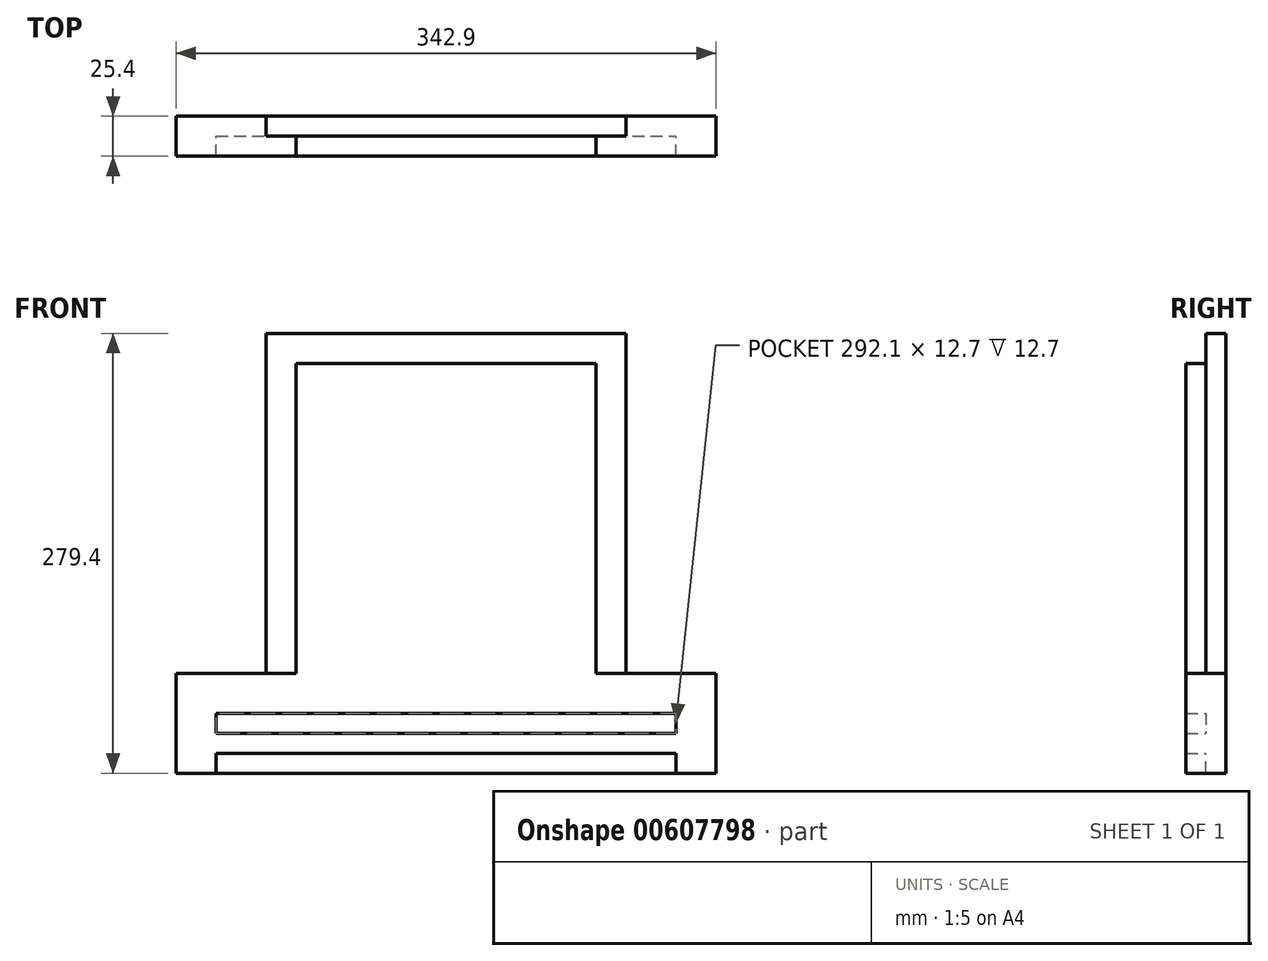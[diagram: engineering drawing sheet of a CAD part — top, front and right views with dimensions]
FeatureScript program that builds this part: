
annotation { "Feature Type Name" : "Feature", "Feature Type Description" : "" }
export const myFeature = defineFeature(function(context is Context, id is Id, definition is map)
    precondition{}
    {
        {
            var Q0;
            Q0=qCreatedBy(makeId("Front.planeOp"),FACE);
            var sketch = newSketch(context, id + "F0", { "sketchPlane" : qUnion([Q0])});
            skLineSegment(sketch, "E0.bottom", {"start": v(0, 0) * mm, "end": v(228.6, 0) * mm});
            skLineSegment(sketch, "E0.top", {"start": v(0, 279.4) * mm, "end": v(228.6, 279.4) * mm});
            skLineSegment(sketch, "E0.left", {"start": v(0, 0) * mm, "end": v(0, 279.4) * mm});
            skLineSegment(sketch, "E0.right", {"start": v(228.6, 0) * mm, "end": v(228.6, 279.4) * mm});
            skSolve(sketch);
        }
        {
            var Q0;
            Q0=makeQuery(id+"F0.imprint","IMPRINT",FACE,{"disambiguationData":[TD([[makeQuery(id+"F0.imprint","IMPRINT",EDGE,{"derivedFrom":sQuery(id+"F0.wireOp",EDGE,"E0.bottom")}),1.0]])]});
            extrude(context, id + "F1", {"entities" : qUnion([Q0]), "depth" : 25.4 * mm, "offsetDistance" : 25.4 * mm});
        }
        {
            var Q0;
            Q0=makeQuery(id+"F1.opExtrude","CAP_FACE",FACE,{"disambiguationData":[OSD([sQuery(id+"F0.wireOp",EDGE,"E0.bottom"),sQuery(id+"F0.wireOp",EDGE,"E0.top"),sQuery(id+"F0.wireOp",EDGE,"E0.left"),sQuery(id+"F0.wireOp",EDGE,"E0.right")])],"isStart":false});
            var sketch = newSketch(context, id + "F2", { "sketchPlane" : qUnion([Q0])});
            skLineSegment(sketch, "E1.bottom", {"start": v(228.6, 0) * mm, "end": v(209.55, 0) * mm});
            skLineSegment(sketch, "E1.top", {"start": v(228.6, 279.4) * mm, "end": v(209.55, 279.4) * mm});
            skLineSegment(sketch, "E1.left", {"start": v(228.6, 0) * mm, "end": v(228.6, 279.4) * mm});
            skLineSegment(sketch, "E1.right", {"start": v(209.55, 0) * mm, "end": v(209.55, 279.4) * mm});
            skSolve(sketch);
        }
        {
            var Q0;
            Q0=makeQuery(id+"F2.imprint","IMPRINT",FACE,{"disambiguationData":[TD([[makeQuery(id+"F2.imprint","IMPRINT",EDGE,{"derivedFrom":sQuery(id+"F2.wireOp",EDGE,"E1.bottom")}),1.0]])]});
            extrude(context, id + "F3", {"entities" : qUnion([Q0]), "operationType" : NewBodyOperationType.REMOVE, "oppositeDirection" : true, "depth" : 12.7 * mm, "offsetDistance" : 25.4 * mm});
        }
        {
            var Q0;
            Q0=makeQuery(id+"F1.opExtrude","CAP_FACE",FACE,{"disambiguationData":[OSD([sQuery(id+"F0.wireOp",EDGE,"E0.bottom"),sQuery(id+"F0.wireOp",EDGE,"E0.top"),sQuery(id+"F0.wireOp",EDGE,"E0.left"),sQuery(id+"F0.wireOp",EDGE,"E0.right")])],"isStart":false});
            var sketch = newSketch(context, id + "F4", { "sketchPlane" : qUnion([Q0])});
            skLineSegment(sketch, "E2.bottom", {"start": v(0, 279.4) * mm, "end": v(19.05, 279.4) * mm});
            skLineSegment(sketch, "E2.top", {"start": v(0, 0) * mm, "end": v(19.05, 0) * mm});
            skLineSegment(sketch, "E2.left", {"start": v(0, 279.4) * mm, "end": v(0, 0) * mm});
            skLineSegment(sketch, "E2.right", {"start": v(19.05, 279.4) * mm, "end": v(19.05, 0) * mm});
            skSolve(sketch);
        }
        {
            var Q0;
            Q0=makeQuery(id+"F4.imprint","IMPRINT",FACE,{"disambiguationData":[TD([[makeQuery(id+"F4.imprint","IMPRINT",EDGE,{"derivedFrom":sQuery(id+"F4.wireOp",EDGE,"E2.bottom")}),-1.0]])]});
            extrude(context, id + "F5", {"entities" : qUnion([Q0]), "operationType" : NewBodyOperationType.REMOVE, "oppositeDirection" : true, "depth" : 12.7 * mm, "offsetDistance" : 25.4 * mm});
        }
        {
            var Q0;
            Q0=makeQuery(id+"F1.opExtrude","CAP_FACE",FACE,{"disambiguationData":[OSD([sQuery(id+"F0.wireOp",EDGE,"E0.bottom"),sQuery(id+"F0.wireOp",EDGE,"E0.top"),sQuery(id+"F0.wireOp",EDGE,"E0.left"),sQuery(id+"F0.wireOp",EDGE,"E0.right")])],"isStart":false});
            var sketch = newSketch(context, id + "F6", { "sketchPlane" : qUnion([Q0])});
            skLineSegment(sketch, "E3.bottom", {"start": v(19.05, 279.4) * mm, "end": v(209.55, 279.4) * mm});
            skLineSegment(sketch, "E3.top", {"start": v(19.05, 260.35) * mm, "end": v(209.55, 260.35) * mm});
            skLineSegment(sketch, "E3.left", {"start": v(19.05, 279.4) * mm, "end": v(19.05, 260.35) * mm});
            skLineSegment(sketch, "E3.right", {"start": v(209.55, 279.4) * mm, "end": v(209.55, 260.35) * mm});
            skSolve(sketch);
        }
        {
            var Q0;
            Q0=makeQuery(id+"F6.imprint","IMPRINT",FACE,{"disambiguationData":[TD([[makeQuery(id+"F6.imprint","IMPRINT",EDGE,{"derivedFrom":sQuery(id+"F6.wireOp",EDGE,"E3.bottom")}),-1.0]])]});
            extrude(context, id + "F7", {"entities" : qUnion([Q0]), "operationType" : NewBodyOperationType.REMOVE, "oppositeDirection" : true, "depth" : 12.7 * mm, "offsetDistance" : 25.4 * mm});
        }
        {
            var Q0;
            Q0=makeQuery(id+"F1.opExtrude","SWEPT_FACE",FACE,{"disambiguationData":[OSD([sQuery(id+"F0.wireOp",EDGE,"E0.right")])]});
            var sketch = newSketch(context, id + "F8", { "sketchPlane" : qUnion([Q0])});
            skLineSegment(sketch, "E4.bottom", {"start": v(0, 0) * mm, "end": v(-12.7, 0) * mm});
            skLineSegment(sketch, "E4.top", {"start": v(0, 63.5) * mm, "end": v(-12.7, 63.5) * mm});
            skLineSegment(sketch, "E4.left", {"start": v(0, 0) * mm, "end": v(0, 63.5) * mm});
            skLineSegment(sketch, "E4.right", {"start": v(-12.7, 0) * mm, "end": v(-12.7, 63.5) * mm});
            skSolve(sketch);
        }
        {
            var Q0;
            Q0=makeQuery(id+"F8.imprint","IMPRINT",FACE,{"disambiguationData":[TD([[makeQuery(id+"F8.imprint","IMPRINT",EDGE,{"derivedFrom":sQuery(id+"F8.wireOp",EDGE,"E4.bottom")}),1.0]])]});
            extrude(context, id + "F9", {"entities" : qUnion([Q0]), "operationType" : NewBodyOperationType.ADD, "depth" : 57.15 * mm, "offsetDistance" : 25.4 * mm});
        }
        {
            var Q0;
            Q0=makeQuery(id+"F1.opExtrude","SWEPT_FACE",FACE,{"disambiguationData":[OSD([sQuery(id+"F0.wireOp",EDGE,"E0.left")])]});
            var sketch = newSketch(context, id + "F10", { "sketchPlane" : qUnion([Q0])});
            skLineSegment(sketch, "E5.bottom", {"start": v(0, 0) * mm, "end": v(12.7, 0) * mm});
            skLineSegment(sketch, "E5.top", {"start": v(0, 63.5) * mm, "end": v(12.7, 63.5) * mm});
            skLineSegment(sketch, "E5.left", {"start": v(0, 0) * mm, "end": v(0, 63.5) * mm});
            skLineSegment(sketch, "E5.right", {"start": v(12.7, 0) * mm, "end": v(12.7, 63.5) * mm});
            skSolve(sketch);
        }
        {
            var Q0;
            Q0=makeQuery(id+"F10.imprint","IMPRINT",FACE,{"disambiguationData":[TD([[makeQuery(id+"F10.imprint","IMPRINT",EDGE,{"derivedFrom":sQuery(id+"F10.wireOp",EDGE,"E5.bottom")}),-1.0]])]});
            extrude(context, id + "F11", {"entities" : qUnion([Q0]), "operationType" : NewBodyOperationType.ADD, "depth" : 57.15 * mm, "offsetDistance" : 25.4 * mm});
        }
        {
            var Q0;
            Q0=makeQuery(id+"F11.boolean.opBoolean","MERGE",FACE,{"derivedFrom":[makeQuery(id+"F9.boolean.opBoolean","MERGE",FACE,{"derivedFrom":[makeQuery(id+"F7.boolean.opBoolean","MERGE",FACE,{"derivedFrom":[makeQuery(id+"F3.boolean.opBoolean","COPY",FACE,{"derivedFrom":makeQuery(id+"F3.opExtrude","CAP_FACE",FACE,{"disambiguationData":[OSD([sQuery(id+"F2.wireOp",EDGE,"E1.bottom"),sQuery(id+"F2.wireOp",EDGE,"E1.top"),sQuery(id+"F2.wireOp",EDGE,"E1.left"),sQuery(id+"F2.wireOp",EDGE,"E1.right")])],"isStart":false})}),makeQuery(id+"F5.boolean.opBoolean","COPY",FACE,{"derivedFrom":makeQuery(id+"F5.opExtrude","CAP_FACE",FACE,{"disambiguationData":[OSD([sQuery(id+"F4.wireOp",EDGE,"E2.bottom"),sQuery(id+"F4.wireOp",EDGE,"E2.top"),sQuery(id+"F4.wireOp",EDGE,"E2.left"),sQuery(id+"F4.wireOp",EDGE,"E2.right")])],"isStart":false})}),makeQuery(id+"F7.opExtrude","CAP_FACE",FACE,{"disambiguationData":[OSD([sQuery(id+"F6.wireOp",EDGE,"E3.bottom"),sQuery(id+"F6.wireOp",EDGE,"E3.top"),sQuery(id+"F6.wireOp",EDGE,"E3.left"),sQuery(id+"F6.wireOp",EDGE,"E3.right")])],"isStart":false})]}),makeQuery(id+"F9.opExtrude","SWEPT_FACE",FACE,{"disambiguationData":[OSD([sQuery(id+"F8.wireOp",EDGE,"E4.right")])]})]}),makeQuery(id+"F11.opExtrude","SWEPT_FACE",FACE,{"disambiguationData":[OSD([sQuery(id+"F10.wireOp",EDGE,"E5.right")])]})]});
            var sketch = newSketch(context, id + "F12", { "sketchPlane" : qUnion([Q0])});
            skLineSegment(sketch, "E6.bottom", {"start": v(-57.15, 63.5) * mm, "end": v(19.05, 63.5) * mm});
            skLineSegment(sketch, "E6.top", {"start": v(-57.15, 0) * mm, "end": v(19.05, 0) * mm});
            skLineSegment(sketch, "E6.left", {"start": v(-57.15, 63.5) * mm, "end": v(-57.15, 0) * mm});
            skLineSegment(sketch, "E6.right", {"start": v(19.05, 63.5) * mm, "end": v(19.05, 0) * mm});
            skLineSegment(sketch, "E7.bottom", {"start": v(285.75, 0) * mm, "end": v(209.55, 0) * mm});
            skLineSegment(sketch, "E7.top", {"start": v(285.75, 63.5) * mm, "end": v(209.55, 63.5) * mm});
            skLineSegment(sketch, "E7.left", {"start": v(285.75, 0) * mm, "end": v(285.75, 63.5) * mm});
            skLineSegment(sketch, "E7.right", {"start": v(209.55, 0) * mm, "end": v(209.55, 63.5) * mm});
            skSolve(sketch);
        }
        {
            var Q0;
            Q0=makeQuery(id+"F12.imprint","IMPRINT",FACE,{"disambiguationData":[TD([[makeQuery(id+"F12.imprint","IMPRINT",EDGE,{"derivedFrom":sQuery(id+"F12.wireOp",EDGE,"E6.top")}),1.0]])]});
            var Q1;
            Q1=makeQuery(id+"F12.imprint","IMPRINT",FACE,{"disambiguationData":[TD([[makeQuery(id+"F12.imprint","IMPRINT",EDGE,{"derivedFrom":sQuery(id+"F12.wireOp",EDGE,"E7.bottom")}),1.0]])]});
            extrude(context, id + "F13", {"entities" : qUnion([Q0, Q1]), "operationType" : NewBodyOperationType.ADD, "depth" : 12.7 * mm, "offsetDistance" : 25.4 * mm});
        }
        {
            var Q0;
            Q0=makeQuery(id+"F13.boolean.opBoolean","MERGE",FACE,{"derivedFrom":[makeQuery(id+"F1.opExtrude","CAP_FACE",FACE,{"disambiguationData":[OSD([sQuery(id+"F0.wireOp",EDGE,"E0.bottom"),sQuery(id+"F0.wireOp",EDGE,"E0.top"),sQuery(id+"F0.wireOp",EDGE,"E0.left"),sQuery(id+"F0.wireOp",EDGE,"E0.right")])],"isStart":false}),makeQuery(id+"F13.opExtrude","CAP_FACE",FACE,{"disambiguationData":[OSD([sQuery(id+"F12.wireOp",EDGE,"E6.bottom"),sQuery(id+"F12.wireOp",EDGE,"E6.top"),sQuery(id+"F12.wireOp",EDGE,"E6.left"),sQuery(id+"F12.wireOp",EDGE,"E6.right")])],"isStart":false}),makeQuery(id+"F13.opExtrude","CAP_FACE",FACE,{"disambiguationData":[OSD([sQuery(id+"F12.wireOp",EDGE,"E7.bottom"),sQuery(id+"F12.wireOp",EDGE,"E7.top"),sQuery(id+"F12.wireOp",EDGE,"E7.left"),sQuery(id+"F12.wireOp",EDGE,"E7.right")])],"isStart":false})]});
            var sketch = newSketch(context, id + "F14", { "sketchPlane" : qUnion([Q0])});
            skLineSegment(sketch, "E8.bottom", {"start": v(-57.15, 0) * mm, "end": v(285.75, 0) * mm});
            skLineSegment(sketch, "E8.top", {"start": v(-57.15, 12.7) * mm, "end": v(285.75, 12.7) * mm});
            skLineSegment(sketch, "E8.left", {"start": v(-57.15, 0) * mm, "end": v(-57.15, 12.7) * mm});
            skLineSegment(sketch, "E8.right", {"start": v(285.75, 0) * mm, "end": v(285.75, 12.7) * mm});
            skLineSegment(sketch, "E9", {"start": v(285.75, 12.7) * mm, "end": v(285.75, 25.4) * mm});
            skLineSegment(sketch, "E10.bottom", {"start": v(285.75, 25.4) * mm, "end": v(-57.15, 25.4) * mm});
            skLineSegment(sketch, "E10.top", {"start": v(285.75, 38.1) * mm, "end": v(-57.15, 38.1) * mm});
            skLineSegment(sketch, "E10.left", {"start": v(285.75, 25.4) * mm, "end": v(285.75, 38.1) * mm});
            skLineSegment(sketch, "E10.right", {"start": v(-57.15, 25.4) * mm, "end": v(-57.15, 38.1) * mm});
            skLineSegment(sketch, "E11", {"start": v(285.75, 38.1) * mm, "end": v(285.75, 50.8) * mm});
            skLineSegment(sketch, "E12.bottom", {"start": v(285.75, 50.8) * mm, "end": v(-57.15, 50.8) * mm});
            skLineSegment(sketch, "E12.top", {"start": v(285.75, 63.5) * mm, "end": v(-57.15, 63.5) * mm});
            skLineSegment(sketch, "E12.left", {"start": v(285.75, 50.8) * mm, "end": v(285.75, 63.5) * mm});
            skLineSegment(sketch, "E12.right", {"start": v(-57.15, 50.8) * mm, "end": v(-57.15, 63.5) * mm});
            skSolve(sketch);
        }
        {
            var Q0;
            Q0=makeQuery(id+"F14.imprint","IMPRINT",FACE,{"disambiguationData":[TD([[makeQuery(id+"F14.imprint","IMPRINT",EDGE,{"derivedFrom":sQuery(id+"F14.wireOp",EDGE,"E12.bottom")}),-1.0]])]});
            var Q1;
            Q1=makeQuery(id+"F14.imprint","IMPRINT",FACE,{"disambiguationData":[TD([[makeQuery(id+"F14.imprint","IMPRINT",EDGE,{"derivedFrom":sQuery(id+"F14.wireOp",EDGE,"E10.bottom")}),-1.0]])]});
            var Q2;
            Q2=makeQuery(id+"F14.imprint","IMPRINT",FACE,{"disambiguationData":[TD([[makeQuery(id+"F14.imprint","IMPRINT",EDGE,{"derivedFrom":sQuery(id+"F14.wireOp",EDGE,"E8.bottom")}),1.0]])]});
            extrude(context, id + "F15", {"entities" : qUnion([Q0, Q1, Q2]), "operationType" : NewBodyOperationType.REMOVE, "oppositeDirection" : true, "depth" : 12.7 * mm, "offsetDistance" : 25.4 * mm});
        }
        {
            var Q0;
            Q0=makeQuery(id+"F15.boolean.opBoolean","MERGE",FACE,{"derivedFrom":[makeQuery(id+"F11.boolean.opBoolean","MERGE",FACE,{"derivedFrom":[makeQuery(id+"F9.boolean.opBoolean","MERGE",FACE,{"derivedFrom":[makeQuery(id+"F7.boolean.opBoolean","MERGE",FACE,{"derivedFrom":[makeQuery(id+"F3.boolean.opBoolean","COPY",FACE,{"derivedFrom":makeQuery(id+"F3.opExtrude","CAP_FACE",FACE,{"disambiguationData":[OSD([sQuery(id+"F2.wireOp",EDGE,"E1.bottom"),sQuery(id+"F2.wireOp",EDGE,"E1.top"),sQuery(id+"F2.wireOp",EDGE,"E1.left"),sQuery(id+"F2.wireOp",EDGE,"E1.right")])],"isStart":false})}),makeQuery(id+"F5.boolean.opBoolean","COPY",FACE,{"derivedFrom":makeQuery(id+"F5.opExtrude","CAP_FACE",FACE,{"disambiguationData":[OSD([sQuery(id+"F4.wireOp",EDGE,"E2.bottom"),sQuery(id+"F4.wireOp",EDGE,"E2.top"),sQuery(id+"F4.wireOp",EDGE,"E2.left"),sQuery(id+"F4.wireOp",EDGE,"E2.right")])],"isStart":false})}),makeQuery(id+"F7.opExtrude","CAP_FACE",FACE,{"disambiguationData":[OSD([sQuery(id+"F6.wireOp",EDGE,"E3.bottom"),sQuery(id+"F6.wireOp",EDGE,"E3.top"),sQuery(id+"F6.wireOp",EDGE,"E3.left"),sQuery(id+"F6.wireOp",EDGE,"E3.right")])],"isStart":false})]}),makeQuery(id+"F9.opExtrude","SWEPT_FACE",FACE,{"disambiguationData":[OSD([sQuery(id+"F8.wireOp",EDGE,"E4.right")])]})]}),makeQuery(id+"F11.opExtrude","SWEPT_FACE",FACE,{"disambiguationData":[OSD([sQuery(id+"F10.wireOp",EDGE,"E5.right")])]})]}),makeQuery(id+"F15.opExtrude","CAP_FACE",FACE,{"disambiguationData":[OSD([sQuery(id+"F14.wireOp",EDGE,"E12.bottom"),sQuery(id+"F14.wireOp",EDGE,"E12.top"),sQuery(id+"F14.wireOp",EDGE,"E12.left"),sQuery(id+"F14.wireOp",EDGE,"E12.right")])],"isStart":false})]});
            var sketch = newSketch(context, id + "F16", { "sketchPlane" : qUnion([Q0])});
            skLineSegment(sketch, "E13.bottom", {"start": v(-57.15, 63.5) * mm, "end": v(-31.75, 63.5) * mm});
            skLineSegment(sketch, "E13.top", {"start": v(-57.15, 50.8) * mm, "end": v(-31.75, 50.8) * mm});
            skLineSegment(sketch, "E13.left", {"start": v(-57.15, 63.5) * mm, "end": v(-57.15, 50.8) * mm});
            skLineSegment(sketch, "E13.right", {"start": v(-31.75, 63.5) * mm, "end": v(-31.75, 50.8) * mm});
            skLineSegment(sketch, "E14.bottom", {"start": v(285.75, 63.5) * mm, "end": v(260.35, 63.5) * mm});
            skLineSegment(sketch, "E14.top", {"start": v(285.75, 50.8) * mm, "end": v(260.35, 50.8) * mm});
            skLineSegment(sketch, "E14.left", {"start": v(285.75, 63.5) * mm, "end": v(285.75, 50.8) * mm});
            skLineSegment(sketch, "E14.right", {"start": v(260.35, 63.5) * mm, "end": v(260.35, 50.8) * mm});
            skLineSegment(sketch, "E15.bottom", {"start": v(-31.75, 63.5) * mm, "end": v(260.35, 63.5) * mm});
            skLineSegment(sketch, "E15.top", {"start": v(-31.75, 50.8) * mm, "end": v(260.35, 50.8) * mm});
            skSolve(sketch);
        }
        {
            var Q0;
            Q0=makeQuery(id+"F15.boolean.opBoolean","COPY",FACE,{"derivedFrom":makeQuery(id+"F15.opExtrude","CAP_FACE",FACE,{"disambiguationData":[OSD([sQuery(id+"F14.wireOp",EDGE,"E10.bottom"),sQuery(id+"F14.wireOp",EDGE,"E10.top"),sQuery(id+"F14.wireOp",EDGE,"E10.left"),sQuery(id+"F14.wireOp",EDGE,"E10.right")])],"isStart":false})});
            var sketch = newSketch(context, id + "F17", { "sketchPlane" : qUnion([Q0])});
            skLineSegment(sketch, "E16.bottom", {"start": v(-57.15, 38.1) * mm, "end": v(-31.75, 38.1) * mm});
            skLineSegment(sketch, "E16.top", {"start": v(-57.15, 25.4) * mm, "end": v(-31.75, 25.4) * mm});
            skLineSegment(sketch, "E16.left", {"start": v(-57.15, 38.1) * mm, "end": v(-57.15, 25.4) * mm});
            skLineSegment(sketch, "E16.right", {"start": v(-31.75, 38.1) * mm, "end": v(-31.75, 25.4) * mm});
            skLineSegment(sketch, "E17.bottom", {"start": v(285.75, 38.1) * mm, "end": v(260.35, 38.1) * mm});
            skLineSegment(sketch, "E17.top", {"start": v(285.75, 25.4) * mm, "end": v(260.35, 25.4) * mm});
            skLineSegment(sketch, "E17.left", {"start": v(285.75, 38.1) * mm, "end": v(285.75, 25.4) * mm});
            skLineSegment(sketch, "E17.right", {"start": v(260.35, 38.1) * mm, "end": v(260.35, 25.4) * mm});
            skSolve(sketch);
        }
        {
            var Q0;
            Q0=makeQuery(id+"F15.boolean.opBoolean","COPY",FACE,{"derivedFrom":makeQuery(id+"F15.opExtrude","CAP_FACE",FACE,{"disambiguationData":[OSD([sQuery(id+"F14.wireOp",EDGE,"E8.bottom"),sQuery(id+"F14.wireOp",EDGE,"E8.top"),sQuery(id+"F14.wireOp",EDGE,"E8.left"),sQuery(id+"F14.wireOp",EDGE,"E8.right")])],"isStart":false})});
            var sketch = newSketch(context, id + "F18", { "sketchPlane" : qUnion([Q0])});
            skLineSegment(sketch, "E18.bottom", {"start": v(-57.15, 0) * mm, "end": v(-31.75, 0) * mm});
            skLineSegment(sketch, "E18.top", {"start": v(-57.15, 12.7) * mm, "end": v(-31.75, 12.7) * mm});
            skLineSegment(sketch, "E18.left", {"start": v(-57.15, 0) * mm, "end": v(-57.15, 12.7) * mm});
            skLineSegment(sketch, "E18.right", {"start": v(-31.75, 0) * mm, "end": v(-31.75, 12.7) * mm});
            skLineSegment(sketch, "E19.bottom", {"start": v(285.75, 0) * mm, "end": v(260.35, 0) * mm});
            skLineSegment(sketch, "E19.top", {"start": v(285.75, 12.7) * mm, "end": v(260.35, 12.7) * mm});
            skLineSegment(sketch, "E19.left", {"start": v(285.75, 0) * mm, "end": v(285.75, 12.7) * mm});
            skLineSegment(sketch, "E19.right", {"start": v(260.35, 0) * mm, "end": v(260.35, 12.7) * mm});
            skSolve(sketch);
        }
        {
            var Q0;
            Q0=makeQuery(id+"F16.imprint","IMPRINT",FACE,{"disambiguationData":[TD([[makeQuery(id+"F16.imprint","IMPRINT",EDGE,{"derivedFrom":sQuery(id+"F16.wireOp",EDGE,"E13.bottom")}),1.0]])]});
            var Q1;
            Q1=makeQuery(id+"F17.imprint","IMPRINT",FACE,{"disambiguationData":[TD([[makeQuery(id+"F17.imprint","IMPRINT",EDGE,{"derivedFrom":sQuery(id+"F17.wireOp",EDGE,"E16.bottom")}),1.0]])]});
            var Q2;
            Q2=makeQuery(id+"F18.imprint","IMPRINT",FACE,{"disambiguationData":[TD([[makeQuery(id+"F18.imprint","IMPRINT",EDGE,{"derivedFrom":sQuery(id+"F18.wireOp",EDGE,"E18.bottom")}),1.0]])]});
            var Q3;
            Q3=makeQuery(id+"F16.imprint","IMPRINT",FACE,{"disambiguationData":[TD([[makeQuery(id+"F16.imprint","IMPRINT",EDGE,{"derivedFrom":sQuery(id+"F16.wireOp",EDGE,"E14.bottom")}),1.0]])]});
            var Q4;
            Q4=makeQuery(id+"F17.imprint","IMPRINT",FACE,{"disambiguationData":[TD([[makeQuery(id+"F17.imprint","IMPRINT",EDGE,{"derivedFrom":sQuery(id+"F17.wireOp",EDGE,"E17.bottom")}),1.0]])]});
            var Q5;
            Q5=makeQuery(id+"F18.imprint","IMPRINT",FACE,{"disambiguationData":[TD([[makeQuery(id+"F18.imprint","IMPRINT",EDGE,{"derivedFrom":sQuery(id+"F18.wireOp",EDGE,"E19.bottom")}),1.0]])]});
            extrude(context, id + "F19", {"entities" : qUnion([Q0, Q1, Q2, Q3, Q4, Q5]), "operationType" : NewBodyOperationType.ADD, "depth" : 12.7 * mm, "offsetDistance" : 25.4 * mm});
        }
        {
            var Q0;
            Q0=makeQuery(id+"F19.opExtrude","SWEPT_FACE",FACE,{"disambiguationData":[OSD([sQuery(id+"F16.wireOp",EDGE,"E13.right")])]});
            extrude(context, id + "F20", {"entities" : qUnion([Q0]), "operationType" : NewBodyOperationType.ADD, "depth" : 304.8 * mm, "offsetDistance" : 25.4 * mm});
        }
    });
